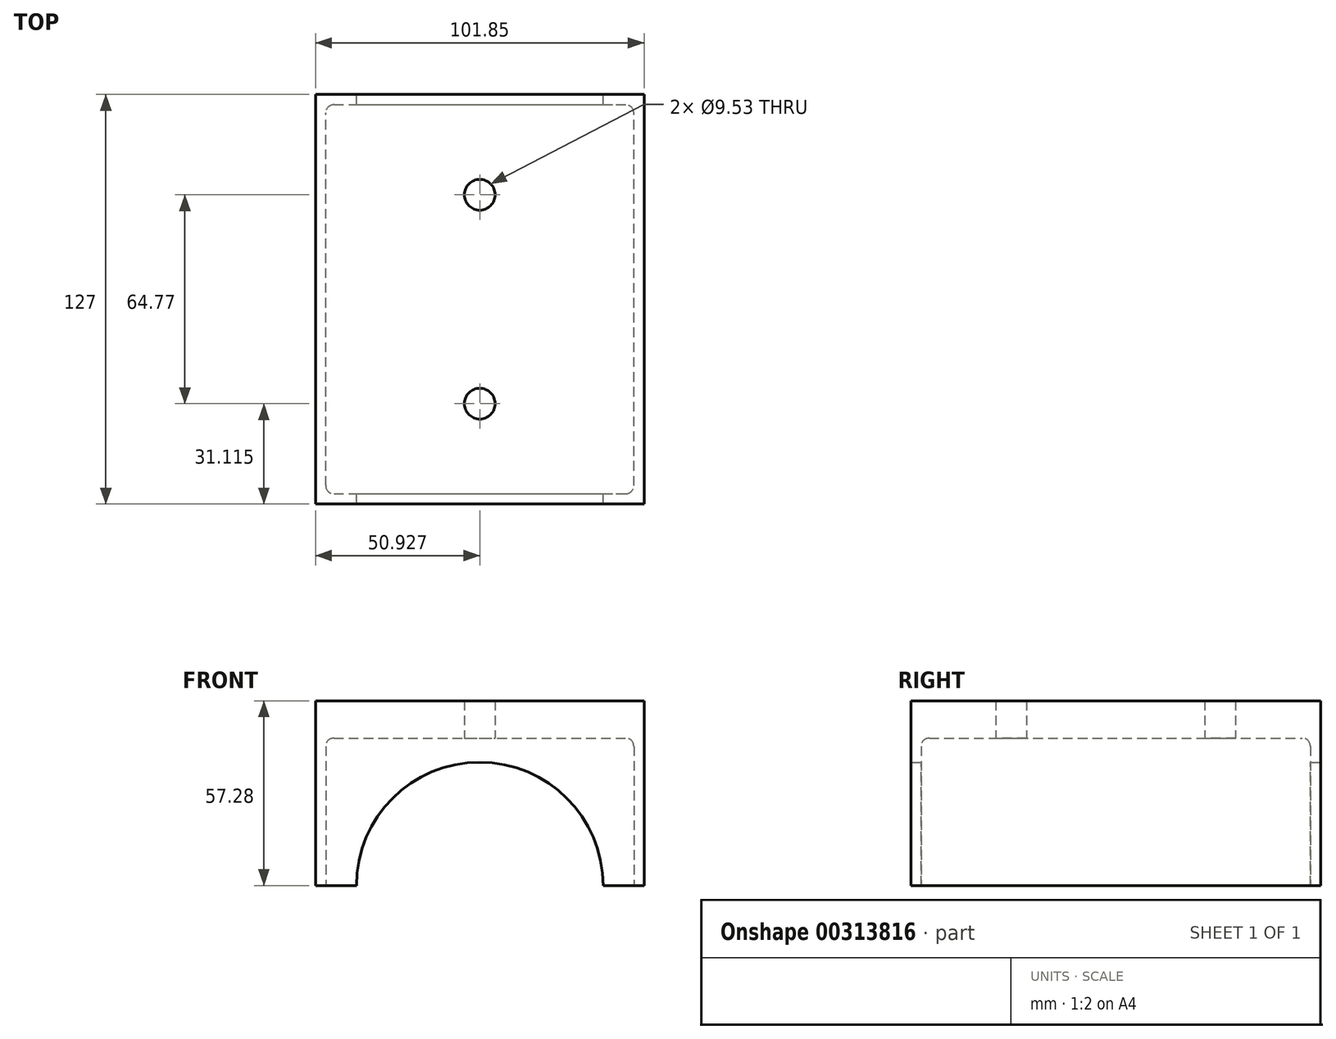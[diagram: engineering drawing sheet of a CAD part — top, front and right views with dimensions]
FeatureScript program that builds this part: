
annotation { "Feature Type Name" : "Feature", "Feature Type Description" : "" }
export const myFeature = defineFeature(function(context is Context, id is Id, definition is map)
    precondition{}
    {
        {
            var Q0;
            Q0=qCreatedBy(makeId("Front.planeOp"),FACE);
            var sketch = newSketch(context, id + "F0", { "sketchPlane" : qUnion([Q0])});
            skLineSegment(sketch, "E0", {"start": v(0, 0) * mm, "end": v(0, 57.28) * mm});
            skLineSegment(sketch, "E1", {"start": v(0, 57.28) * mm, "end": v(101.85, 57.28) * mm});
            skLineSegment(sketch, "E2", {"start": v(101.85, 57.28) * mm, "end": v(101.85, 0) * mm});
            skLineSegment(sketch, "E3", {"start": v(101.85, 0) * mm, "end": v(89.15, 0) * mm});
            skLineSegment(sketch, "E4", {"start": v(50.93, 0) * mm, "end": v(50.93, 57.28) * mm, "construction": true});
            skPoint(sketch, "E4.startSnap0", {"position": v(50.93, 57.28) * mm});
            skLineSegment(sketch, "E5.MirrorCS", {"start": v(0, 0) * mm, "end": v(12.7, 0) * mm});
            skArc(sketch, "E6", {"start": v(89.15, 0) * mm, "mid": v(50.93, 38.23) * mm, "end": v(12.7, 0) * mm});
            skSolve(sketch);
        }
        {
            var Q0;
            Q0 = qSketchRegion(id + "F0", true);
            extrude(context, id + "F1", {"entities" : qUnion([Q0]), "depth" : 127 * mm, "offsetDistance" : 25.4 * mm});
        }
        {
            var Q0;
            Q0=makeQuery(id+"F1.opExtrude","SWEPT_FACE",FACE,{"disambiguationData":[OSD([sQuery(id+"F0.wireOp",EDGE,"E5.MirrorCS")])]});
            var sketch = newSketch(context, id + "F2", { "sketchPlane" : qUnion([Q0])});
            skSolve(sketch);
        }
        {
            var Q0;
            {var subQ0=sQuery(id+"F0.wireOp",EDGE,"E5.MirrorCS");Q0=makeQuery(id+"F2.imprint","IMPRINT",FACE,{"disambiguationData":[TD([[makeQuery(id+"F2.imprint","IMPRINT",EDGE,{"derivedFrom":makeQuery(id+"F1.opExtrude","CAP_EDGE",EDGE,{"disambiguationData":[OSD([subQ0])],"isStart":true})}),1.0]])]});}
            var sketch = newSketch(context, id + "F3", { "sketchPlane" : qUnion([Q0])});
            skLineSegment(sketch, "E7.0", {"start": v(3.18, 127) * mm, "end": v(3.18, 0) * mm});
            skLineSegment(sketch, "E8.0", {"start": v(12.7, 127) * mm, "end": v(89.15, 127) * mm, "construction": true});
            skLineSegment(sketch, "E9", {"start": v(50.93, 127) * mm, "end": v(50.93, 0) * mm, "construction": true});
            skLineSegment(sketch, "E10", {"start": v(3.18, 123.83) * mm, "end": v(50.93, 123.83) * mm});
            skLineSegment(sketch, "E11", {"start": v(3.18, 3.17) * mm, "end": v(50.93, 3.17) * mm});
            skLineSegment(sketch, "E12.MirrorCS", {"start": v(98.68, 123.83) * mm, "end": v(50.93, 123.83) * mm});
            skLineSegment(sketch, "E13.MirrorCS", {"start": v(98.68, 127) * mm, "end": v(98.68, 0) * mm});
            skLineSegment(sketch, "E14.MirrorCS", {"start": v(98.68, 3.17) * mm, "end": v(50.93, 3.17) * mm});
            skSolve(sketch);
        }
        {
            var Q0;
            Q0 = qSketchRegion(id + "F3", true);
            extrude(context, id + "F4", {"entities" : qUnion([Q0]), "operationType" : NewBodyOperationType.REMOVE, "oppositeDirection" : true, "depth" : 45.72 * mm, "offsetDistance" : 25.4 * mm});
        }
        {
            var Q0;
            Q0=makeQuery(id+"F4.boolean.opBoolean","COPY",EDGE,{"derivedFrom":makeQuery(id+"F4.opExtrude","CAP_EDGE",EDGE,{"disambiguationData":[OSD([sQuery(id+"F3.wireOp",EDGE,"E7.0")])],"isStart":false})});
            var Q1;
            Q1=makeQuery(id+"F4.boolean.opBoolean","COPY",EDGE,{"derivedFrom":makeQuery(id+"F4.opExtrude","CAP_EDGE",EDGE,{"disambiguationData":[OSD([sQuery(id+"F3.wireOp",EDGE,"E13.MirrorCS")])],"isStart":false})});
            var Q2;
            Q2=makeQuery(id+"F4.boolean.opBoolean","COPY",EDGE,{"derivedFrom":makeQuery(id+"F4.opExtrude","CAP_EDGE",EDGE,{"disambiguationData":[OSD([sQuery(id+"F3.wireOp",EDGE,"E10"),sQuery(id+"F3.wireOp",EDGE,"E12.MirrorCS")])],"isStart":false})});
            var Q3;
            Q3=makeQuery(id+"F4.boolean.opBoolean","COPY",EDGE,{"derivedFrom":makeQuery(id+"F4.opExtrude","SWEPT_EDGE",EDGE,{"disambiguationData":[OSD([sQuery(id+"F3.wireOp",EDGE,"E12.MirrorCS"),sQuery(id+"F3.wireOp",EDGE,"E13.MirrorCS")])]})});
            var Q4;
            Q4=makeQuery(id+"F4.boolean.opBoolean","COPY",EDGE,{"derivedFrom":makeQuery(id+"F4.opExtrude","SWEPT_EDGE",EDGE,{"disambiguationData":[OSD([sQuery(id+"F3.wireOp",EDGE,"E7.0"),sQuery(id+"F3.wireOp",EDGE,"E10")])]})});
            var Q5;
            Q5=makeQuery(id+"F4.boolean.opBoolean","COPY",EDGE,{"derivedFrom":makeQuery(id+"F4.opExtrude","SWEPT_EDGE",EDGE,{"disambiguationData":[OSD([sQuery(id+"F3.wireOp",EDGE,"E13.MirrorCS"),sQuery(id+"F3.wireOp",EDGE,"E14.MirrorCS")])]})});
            var Q6;
            Q6=makeQuery(id+"F4.boolean.opBoolean","COPY",EDGE,{"derivedFrom":makeQuery(id+"F4.opExtrude","CAP_EDGE",EDGE,{"disambiguationData":[OSD([sQuery(id+"F3.wireOp",EDGE,"E11"),sQuery(id+"F3.wireOp",EDGE,"E14.MirrorCS")])],"isStart":false})});
            var Q7;
            Q7=makeQuery(id+"F4.boolean.opBoolean","COPY",EDGE,{"derivedFrom":makeQuery(id+"F4.opExtrude","SWEPT_EDGE",EDGE,{"disambiguationData":[OSD([sQuery(id+"F3.wireOp",EDGE,"E7.0"),sQuery(id+"F3.wireOp",EDGE,"E11")])]})});
            fillet(context, id + "F5", {"entities" : qUnion([Q0, Q1, Q2, Q3, Q4, Q5, Q6, Q7]), "tangentPropagation" : true, "radius" : 2.54 * mm, "defaultsChanged" : true, "vertexSettings" : [], "allowEdgeOverflow" : false});
        }
        {
            var Q0;
            Q0=makeQuery(id+"F4.boolean.opBoolean","COPY",FACE,{"derivedFrom":makeQuery(id+"F4.opExtrude","CAP_FACE",FACE,{"disambiguationData":[OSD([sQuery(id+"F3.wireOp",EDGE,"E7.0"),sQuery(id+"F3.wireOp",EDGE,"E10"),sQuery(id+"F3.wireOp",EDGE,"E11"),sQuery(id+"F3.wireOp",EDGE,"E12.MirrorCS"),sQuery(id+"F3.wireOp",EDGE,"E13.MirrorCS"),sQuery(id+"F3.wireOp",EDGE,"E14.MirrorCS")])],"isStart":false})});
            var sketch = newSketch(context, id + "F6", { "sketchPlane" : qUnion([Q0])});
            skCircle(sketch, "E15", {"center": v(50.93, 95.88) * mm, "radius": 4.76 * mm});
            skPoint(sketch, "E15.centerSnap0", {"position": v(50.93, 121.29) * mm});
            skCircle(sketch, "E16", {"center": v(50.93, 31.12) * mm, "radius": 4.76 * mm});
            skSolve(sketch);
        }
        {
            var Q0;
            Q0 = qSketchRegion(id + "F6", true);
            extrude(context, id + "F7", {"entities" : qUnion([Q0]), "operationType" : NewBodyOperationType.REMOVE, "endBound" : BoundingType.UP_TO_NEXT, "oppositeDirection" : true, "depth" : 25.4 * mm, "offsetDistance" : 25.4 * mm});
        }
    });
